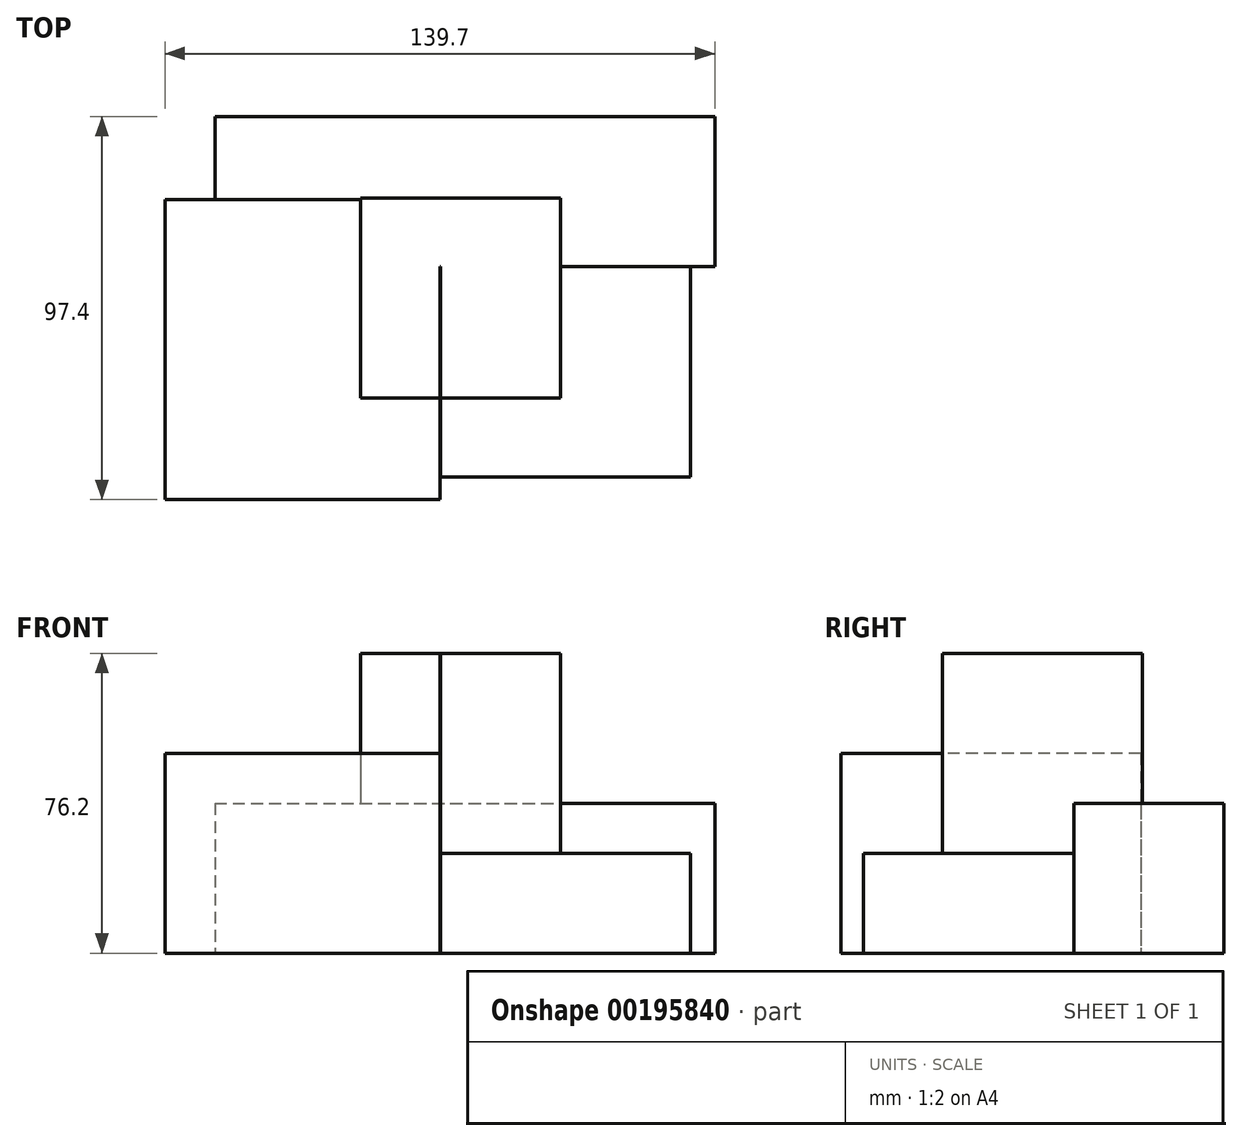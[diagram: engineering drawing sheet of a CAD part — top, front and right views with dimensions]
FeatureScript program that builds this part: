
annotation { "Feature Type Name" : "Feature", "Feature Type Description" : "" }
export const myFeature = defineFeature(function(context is Context, id is Id, definition is map)
    precondition{}
    {
        {
            var Q0;
            Q0=qCreatedBy(makeId("Top.planeOp"),FACE);
            var sketch = newSketch(context, id + "F0", { "sketchPlane" : qUnion([Q0])});
            skLineSegment(sketch, "E0.bottom", {"start": v(-85.34, 24.95) * mm, "end": v(-15.49, 24.95) * mm});
            skLineSegment(sketch, "E0.top", {"start": v(-85.34, -51.25) * mm, "end": v(-15.49, -51.25) * mm});
            skLineSegment(sketch, "E0.left", {"start": v(-85.34, 24.95) * mm, "end": v(-85.34, -51.25) * mm});
            skLineSegment(sketch, "E0.right", {"start": v(-15.49, 24.95) * mm, "end": v(-15.49, -51.25) * mm});
            skLineSegment(sketch, "E1.bottom", {"start": v(-72.64, 8.05) * mm, "end": v(54.36, 8.05) * mm});
            skLineSegment(sketch, "E1.top", {"start": v(-72.64, 46.15) * mm, "end": v(54.36, 46.15) * mm});
            skLineSegment(sketch, "E1.left", {"start": v(-72.64, 8.05) * mm, "end": v(-72.64, 46.15) * mm});
            skLineSegment(sketch, "E1.right", {"start": v(54.36, 8.05) * mm, "end": v(54.36, 46.15) * mm});
            skLineSegment(sketch, "E2.bottom", {"start": v(48.13, 18.07) * mm, "end": v(-15.37, 18.07) * mm});
            skLineSegment(sketch, "E2.top", {"start": v(48.13, -45.43) * mm, "end": v(-15.37, -45.43) * mm});
            skLineSegment(sketch, "E2.left", {"start": v(48.13, 18.07) * mm, "end": v(48.13, -45.43) * mm});
            skLineSegment(sketch, "E2.right", {"start": v(-15.37, 18.07) * mm, "end": v(-15.37, -45.43) * mm});
            skLineSegment(sketch, "E3.bottom", {"start": v(-35.65, 25.4) * mm, "end": v(15.15, 25.4) * mm});
            skLineSegment(sketch, "E3.top", {"start": v(-35.65, -25.4) * mm, "end": v(15.15, -25.4) * mm});
            skLineSegment(sketch, "E3.left", {"start": v(-35.65, 25.4) * mm, "end": v(-35.65, -25.4) * mm});
            skLineSegment(sketch, "E3.right", {"start": v(15.15, 25.4) * mm, "end": v(15.15, -25.4) * mm});
            skPoint(sketch, "E3.middle", {"position": v(-10.25, 0) * mm});
            skSolve(sketch);
        }
        {
            var Q0;
            {var subQ0=sQuery(id+"F0.wireOp",EDGE,"E0.right");var subQ1=sQuery(id+"F0.wireOp",EDGE,"E0.bottom");var subQ2=makeQuery(id+"F0.imprint","INTERSECT",VERTEX,{"derivedFrom":[subQ1,subQ0]});Q0=makeQuery(id+"F0.imprint","IMPRINT",FACE,{"disambiguationData":[TD([[makeQuery(id+"F0.imprint","IMPRINT",EDGE,{"disambiguationData":[TD([[subQ2,1.0]])],"derivedFrom":subQ1}),-1.0]])]});}
            var Q1;
            {var subQ6=sQuery(id+"F0.wireOp",EDGE,"E3.bottom");Q1=makeQuery(id+"F0.imprint","IMPRINT",FACE,{"disambiguationData":[TD([[makeQuery(id+"F0.imprint","IMPRINT",EDGE,{"derivedFrom":subQ6}),-1.0]])]});}
            var Q2;
            {var subQ0=sQuery(id+"F0.wireOp",EDGE,"E2.right");var subQ1=sQuery(id+"F0.wireOp",EDGE,"E1.bottom");var subQ2=makeQuery(id+"F0.imprint","INTERSECT",VERTEX,{"derivedFrom":[subQ1,subQ0]});Q2=makeQuery(id+"F0.imprint","IMPRINT",FACE,{"disambiguationData":[TD([[makeQuery(id+"F0.imprint","IMPRINT",EDGE,{"disambiguationData":[TD([[subQ2,-1.0]])],"derivedFrom":subQ1}),1.0]])]});}
            var Q3;
            {var subQ0=sQuery(id+"F0.wireOp",EDGE,"E2.right");var subQ1=sQuery(id+"F0.wireOp",EDGE,"E1.bottom");var subQ2=makeQuery(id+"F0.imprint","INTERSECT",VERTEX,{"derivedFrom":[subQ1,subQ0]});Q3=makeQuery(id+"F0.imprint","IMPRINT",FACE,{"disambiguationData":[TD([[makeQuery(id+"F0.imprint","IMPRINT",EDGE,{"disambiguationData":[TD([[subQ2,-1.0]])],"derivedFrom":subQ1}),-1.0]])]});}
            var Q4;
            {var subQ0=sQuery(id+"F0.wireOp",EDGE,"E3.top");var subQ1=sQuery(id+"F0.wireOp",EDGE,"E0.right");var subQ2=makeQuery(id+"F0.imprint","INTERSECT",VERTEX,{"derivedFrom":[subQ1,subQ0]});Q4=makeQuery(id+"F0.imprint","IMPRINT",FACE,{"disambiguationData":[TD([[makeQuery(id+"F0.imprint","IMPRINT",EDGE,{"disambiguationData":[TD([[subQ2,1.0]])],"derivedFrom":subQ1}),-1.0]])]});}
            extrude(context, id + "F1", {"entities" : qUnion([Q0, Q1, Q2, Q3, Q4]), "depth" : 76.2 * mm});
        }
        {
            var Q0;
            {var subQ1=sQuery(id+"F0.wireOp",EDGE,"E0.top");Q0=makeQuery(id+"F0.imprint","IMPRINT",FACE,{"disambiguationData":[TD([[makeQuery(id+"F0.imprint","IMPRINT",EDGE,{"derivedFrom":subQ1}),1.0]])]});}
            var Q1;
            {var subQ0=sQuery(id+"F0.wireOp",EDGE,"E1.left");var subQ1=sQuery(id+"F0.wireOp",EDGE,"E0.bottom");var subQ2=makeQuery(id+"F0.imprint","INTERSECT",VERTEX,{"derivedFrom":[subQ1,subQ0]});Q1=makeQuery(id+"F0.imprint","IMPRINT",FACE,{"disambiguationData":[TD([[makeQuery(id+"F0.imprint","IMPRINT",EDGE,{"disambiguationData":[TD([[subQ2,-1.0]])],"derivedFrom":subQ1}),-1.0]])]});}
            extrude(context, id + "F2", {"entities" : qUnion([Q0, Q1]), "operationType" : NewBodyOperationType.ADD, "depth" : 50.8 * mm});
        }
        {
            var Q0;
            {var subQ0=sQuery(id+"F0.wireOp",EDGE,"E1.top");Q0=makeQuery(id+"F0.imprint","IMPRINT",FACE,{"disambiguationData":[TD([[makeQuery(id+"F0.imprint","IMPRINT",EDGE,{"derivedFrom":subQ0}),-1.0]])]});}
            var Q1;
            {var subQ0=sQuery(id+"F0.wireOp",EDGE,"E2.left");var subQ1=sQuery(id+"F0.wireOp",EDGE,"E1.bottom");var subQ2=makeQuery(id+"F0.imprint","INTERSECT",VERTEX,{"derivedFrom":[subQ1,subQ0]});Q1=makeQuery(id+"F0.imprint","IMPRINT",FACE,{"disambiguationData":[TD([[makeQuery(id+"F0.imprint","IMPRINT",EDGE,{"disambiguationData":[TD([[subQ2,1.0]])],"derivedFrom":subQ1}),1.0]])]});}
            extrude(context, id + "F3", {"entities" : qUnion([Q0, Q1]), "operationType" : NewBodyOperationType.ADD, "depth" : 38.1 * mm});
        }
        {
            var Q0;
            {var subQ1=sQuery(id+"F0.wireOp",EDGE,"E2.top");Q0=makeQuery(id+"F0.imprint","IMPRINT",FACE,{"disambiguationData":[TD([[makeQuery(id+"F0.imprint","IMPRINT",EDGE,{"derivedFrom":subQ1}),-1.0]])]});}
            extrude(context, id + "F4", {"entities" : qUnion([Q0]), "operationType" : NewBodyOperationType.ADD, "depth" : 25.4 * mm});
        }
    });
